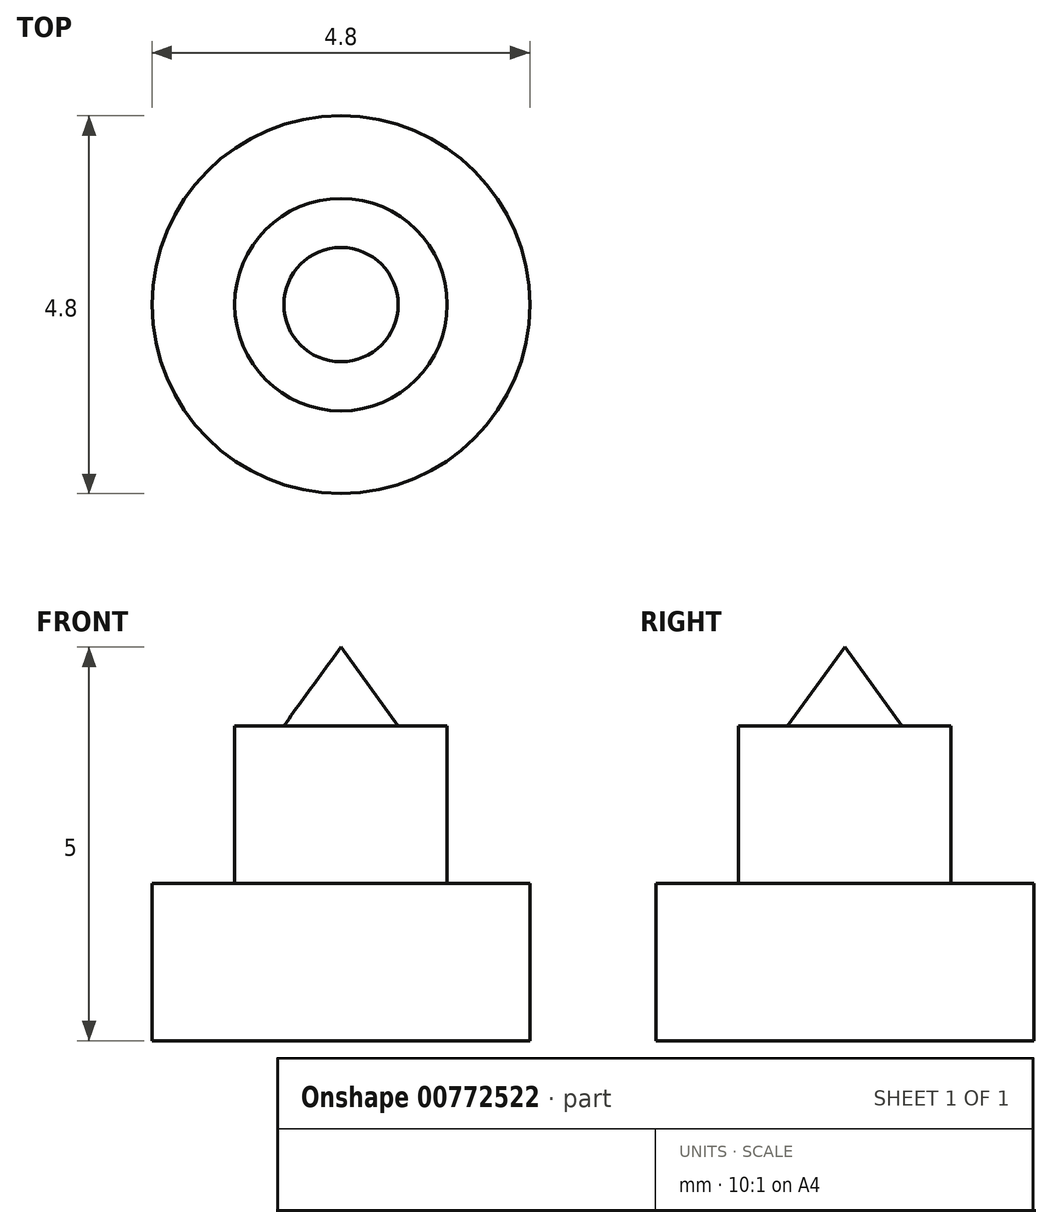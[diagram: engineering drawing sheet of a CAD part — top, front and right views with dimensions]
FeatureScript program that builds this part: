
annotation { "Feature Type Name" : "Feature", "Feature Type Description" : "" }
export const myFeature = defineFeature(function(context is Context, id is Id, definition is map)
    precondition{}
    {
        {
            var Q0;
            Q0=qCreatedBy(makeId("Top.planeOp"),FACE);
            var sketch = newSketch(context, id + "F0", { "sketchPlane" : qUnion([Q0])});
            skCircle(sketch, "E0", {"center": v(0, 0) * mm, "radius": 2.4 * mm});
            skCircle(sketch, "E1", {"center": v(0, 0) * mm, "radius": 1.35 * mm});
            skSolve(sketch);
        }
        {
            var Q0;
            Q0=makeQuery(id+"F0.imprint","IMPRINT",FACE,{"disambiguationData":[TD([[makeQuery(id+"F0.imprint","IMPRINT",EDGE,{"derivedFrom":sQuery(id+"F0.wireOp",EDGE,"E1")}),1.0]])]});
            extrude(context, id + "F1", {"entities" : qUnion([Q0]), "depth" : 4 * mm, "offsetDistance" : 25 * mm});
        }
        {
            var Q0;
            Q0=qSketchRegion(id+"F0",true);
            extrude(context, id + "F2", {"entities" : qUnion([Q0]), "operationType" : NewBodyOperationType.ADD, "depth" : 2 * mm, "offsetDistance" : 25 * mm});
        }
        {
            var Q0;
            Q0=makeQuery(id+"F1.opExtrude","CAP_FACE",FACE,{"disambiguationData":[OSD([sQuery(id+"F0.wireOp",EDGE,"E1")])],"isStart":false});
            var sketch = newSketch(context, id + "F3", { "sketchPlane" : qUnion([Q0])});
            skCircle(sketch, "E2", {"center": v(0, 0) * mm, "radius": 1 * mm});
            skSolve(sketch);
        }
        {
            var Q0;
            Q0=qCreatedBy(makeId("Right.planeOp"),FACE);
            var sketch = newSketch(context, id + "F4", { "sketchPlane" : qUnion([Q0])});
            skLineSegment(sketch, "E3", {"start": v(0, 4) * mm, "end": v(0.73, 4) * mm});
            skLineSegment(sketch, "E4", {"start": v(0.73, 4) * mm, "end": v(0, 5) * mm});
            skLineSegment(sketch, "E5", {"start": v(0, 5) * mm, "end": v(0, 4) * mm});
            skSolve(sketch);
        }
        {
            var Q0;
            Q0=makeQuery(id+"F4.imprint","IMPRINT",FACE,{"disambiguationData":[TD([[makeQuery(id+"F4.imprint","IMPRINT",EDGE,{"derivedFrom":sQuery(id+"F4.wireOp",EDGE,"E3")}),1.0]])]});
            var Q1;
            Q1=sQuery(id+"F4.wireOp",EDGE,"E5");
            revolve(context, id + "F5", {"surfaceOperationType" : NewSurfaceOperationType.NEW, "entities" : qUnion([Q0]), "axis" : qUnion([Q1]), "revolveType" : RevolveType.FULL});
        }
    });
